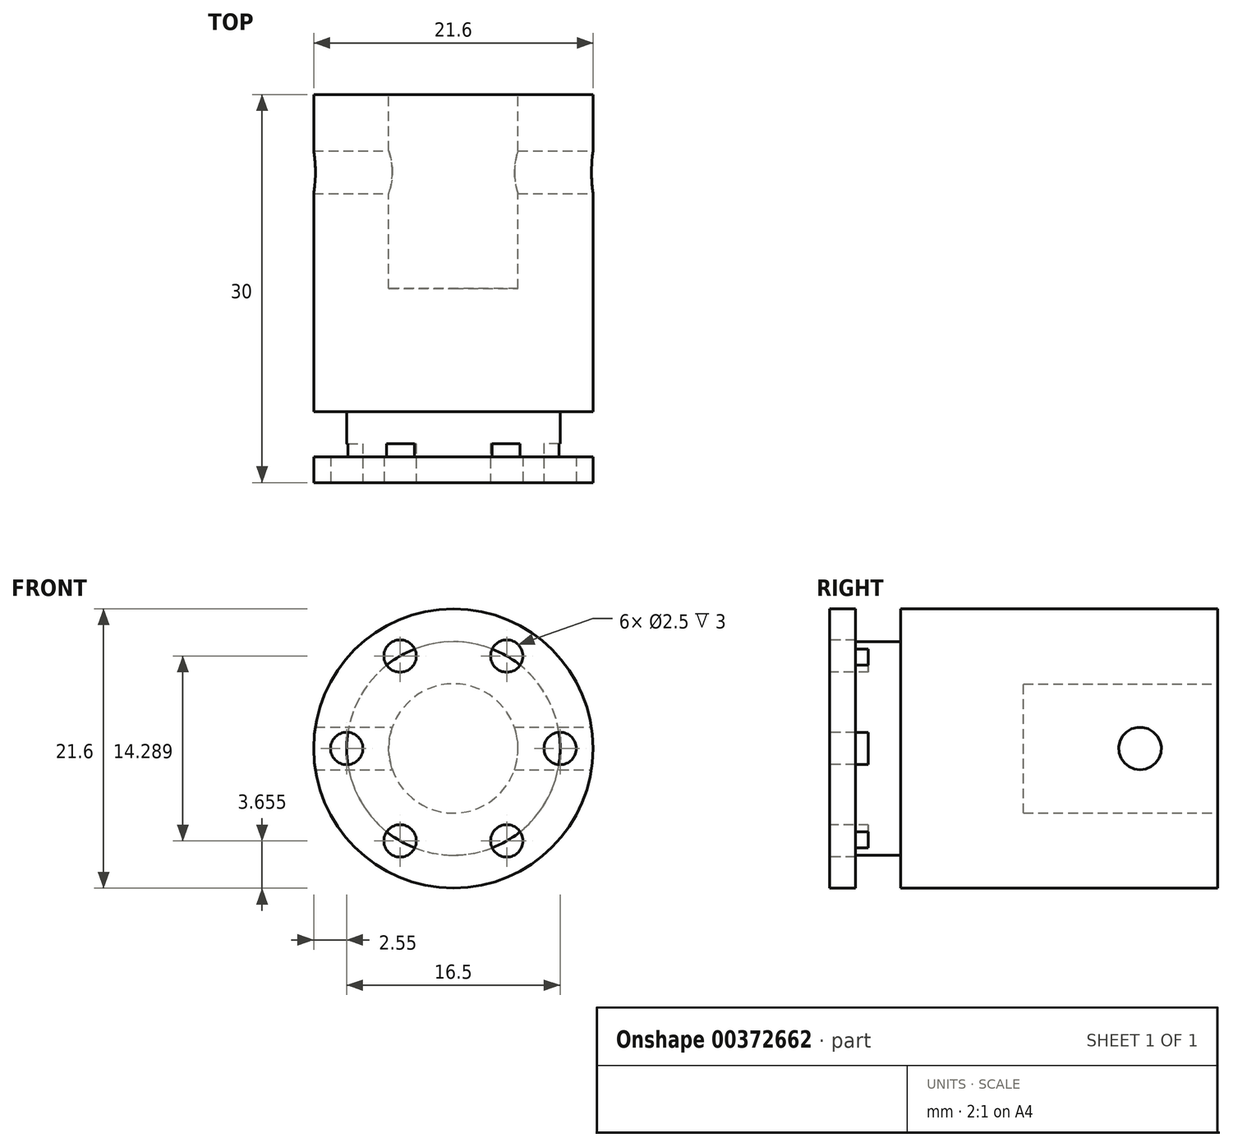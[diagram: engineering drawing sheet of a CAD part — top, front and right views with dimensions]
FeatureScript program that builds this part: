
annotation { "Feature Type Name" : "Feature", "Feature Type Description" : "" }
export const myFeature = defineFeature(function(context is Context, id is Id, definition is map)
    precondition{}
    {
        {
            var Q0;
            Q0=qCreatedBy(makeId("Front.planeOp"),FACE);
            var sketch = newSketch(context, id + "F0", { "sketchPlane" : qUnion([Q0])});
            skCircle(sketch, "E0", {"center": v(0, 0) * mm, "radius": 10.8 * mm});
            skCircle(sketch, "E1", {"center": v(0, 0) * mm, "radius": 5 * mm});
            skSolve(sketch);
        }
        {
            var Q0;
            Q0=makeQuery(id+"F0.imprint","IMPRINT",FACE,{"disambiguationData":[TD([[makeQuery(id+"F0.imprint","IMPRINT",EDGE,{"derivedFrom":sQuery(id+"F0.wireOp",EDGE,"E0")}),1.0]])]});
            var Q1;
            Q1=makeQuery(id+"F0.imprint","IMPRINT",FACE,{"disambiguationData":[TD([[makeQuery(id+"F0.imprint","IMPRINT",EDGE,{"derivedFrom":sQuery(id+"F0.wireOp",EDGE,"E1")}),1.0]])]});
            extrude(context, id + "F1", {"entities" : qUnion([Q0, Q1]), "depth" : 30 * mm, "offsetDistance" : 25 * mm});
        }
        {
            var Q0;
            Q0=makeQuery(id+"F0.imprint","IMPRINT",FACE,{"disambiguationData":[TD([[makeQuery(id+"F0.imprint","IMPRINT",EDGE,{"derivedFrom":sQuery(id+"F0.wireOp",EDGE,"E1")}),1.0]])]});
            extrude(context, id + "F2", {"entities" : qUnion([Q0]), "operationType" : NewBodyOperationType.REMOVE, "depth" : 15 * mm, "offsetDistance" : 25 * mm});
        }
        {
            var Q0;
            Q0=qCreatedBy(makeId("Right.planeOp"),FACE);
            var sketch = newSketch(context, id + "F3", { "sketchPlane" : qUnion([Q0])});
            skCircle(sketch, "E2", {"center": v(-6, 0) * mm, "radius": 1.65 * mm});
            skCircle(sketch, "E3", {"center": v(-6, 0) * mm, "radius": 2.1 * mm});
            skLineSegment(sketch, "E4", {"start": v(0, 0) * mm, "end": v(-6, 0) * mm, "construction": true});
            skSolve(sketch);
        }
        {
            var Q0;
            Q0=makeQuery(id+"F3.imprint","IMPRINT",FACE,{"disambiguationData":[TD([[makeQuery(id+"F3.imprint","IMPRINT",EDGE,{"derivedFrom":sQuery(id+"F3.wireOp",EDGE,"E2")}),1.0]])]});
            extrude(context, id + "F4", {"entities" : qUnion([Q0]), "operationType" : NewBodyOperationType.REMOVE, "endBound" : BoundingType.THROUGH_ALL, "oppositeDirection" : true, "depth" : 25 * mm, "offsetDistance" : 25 * mm, "hasSecondDirection" : true, "secondDirectionBound" : BoundingType.THROUGH_ALL, "secondDirectionOppositeDirection" : false, "secondDirectionDepth" : 25 * mm});
        }
        {
            var Q0;
            Q0=makeQuery(id+"F1.opExtrude","CAP_FACE",FACE,{"disambiguationData":[OSD([sQuery(id+"F0.wireOp",EDGE,"E0")])],"isStart":false});
            cPlane(context, id + "F5", {"entities" : qUnion([Q0]), "cplaneType" : CPlaneType.OFFSET, "offset" : 2 * mm, "oppositeDirection" : true, "width" : 150 * mm, "height" : 150 * mm});
        }
        {
            var Q0;
            Q0=qCreatedBy(id+"F5.planeOp",FACE);
            var sketch = newSketch(context, id + "F6", { "sketchPlane" : qUnion([Q0])});
            skCircle(sketch, "E5", {"center": v(0, 0) * mm, "radius": 8.25 * mm});
            skCircle(sketch, "E6.0", {"center": v(0, 0) * mm, "radius": 10.8 * mm});
            skSolve(sketch);
        }
        {
            var Q0;
            Q0 = qSketchRegion(id + "F6", true);
            extrude(context, id + "F7", {"entities" : qUnion([Q0]), "operationType" : NewBodyOperationType.REMOVE, "oppositeDirection" : true, "depth" : 3.5 * mm, "offsetDistance" : 25 * mm});
        }
        {
            var Q0;
            Q0=makeQuery(id+"F1.opExtrude","CAP_FACE",FACE,{"disambiguationData":[OSD([sQuery(id+"F0.wireOp",EDGE,"E0")])],"isStart":false});
            var sketch = newSketch(context, id + "F8", { "sketchPlane" : qUnion([Q0])});
            skCircle(sketch, "E7", {"center": v(-8.25, 0) * mm, "radius": 1.25 * mm});
            skCircle(sketch, "E8.1.0", {"center": v(-4.13, -7.14) * mm, "radius": 1.25 * mm});
            skCircle(sketch, "E8.2.0", {"center": v(4.12, -7.14) * mm, "radius": 1.25 * mm});
            skCircle(sketch, "E8.3.0", {"center": v(8.25, 0) * mm, "radius": 1.25 * mm});
            skCircle(sketch, "E8.4.0", {"center": v(4.13, 7.14) * mm, "radius": 1.25 * mm});
            skCircle(sketch, "E8.5.0", {"center": v(-4.13, 7.14) * mm, "radius": 1.25 * mm});
            skPoint(sketch, "E8.center", {"position": v(0, 0) * mm});
            skSolve(sketch);
        }
        {
            var Q0;
            Q0=makeQuery(id+"F8.imprint","IMPRINT",FACE,{"disambiguationData":[TD([[makeQuery(id+"F8.imprint","IMPRINT",EDGE,{"derivedFrom":sQuery(id+"F8.wireOp",EDGE,"E8.5.0")}),1.0]])]});
            var Q1;
            Q1=makeQuery(id+"F8.imprint","IMPRINT",FACE,{"disambiguationData":[TD([[makeQuery(id+"F8.imprint","IMPRINT",EDGE,{"derivedFrom":sQuery(id+"F8.wireOp",EDGE,"E8.4.0")}),1.0]])]});
            var Q2;
            Q2=makeQuery(id+"F8.imprint","IMPRINT",FACE,{"disambiguationData":[TD([[makeQuery(id+"F8.imprint","IMPRINT",EDGE,{"derivedFrom":sQuery(id+"F8.wireOp",EDGE,"E7")}),1.0]])]});
            var Q3;
            Q3=makeQuery(id+"F8.imprint","IMPRINT",FACE,{"disambiguationData":[TD([[makeQuery(id+"F8.imprint","IMPRINT",EDGE,{"derivedFrom":sQuery(id+"F8.wireOp",EDGE,"E8.1.0")}),1.0]])]});
            var Q4;
            Q4=makeQuery(id+"F8.imprint","IMPRINT",FACE,{"disambiguationData":[TD([[makeQuery(id+"F8.imprint","IMPRINT",EDGE,{"derivedFrom":sQuery(id+"F8.wireOp",EDGE,"E8.2.0")}),1.0]])]});
            var Q5;
            Q5=makeQuery(id+"F8.imprint","IMPRINT",FACE,{"disambiguationData":[TD([[makeQuery(id+"F8.imprint","IMPRINT",EDGE,{"derivedFrom":sQuery(id+"F8.wireOp",EDGE,"E8.3.0")}),1.0]])]});
            extrude(context, id + "F9", {"entities" : qUnion([Q0, Q1, Q2, Q3, Q4, Q5]), "operationType" : NewBodyOperationType.REMOVE, "oppositeDirection" : true, "depth" : 3 * mm, "offsetDistance" : 25 * mm});
        }
    });
